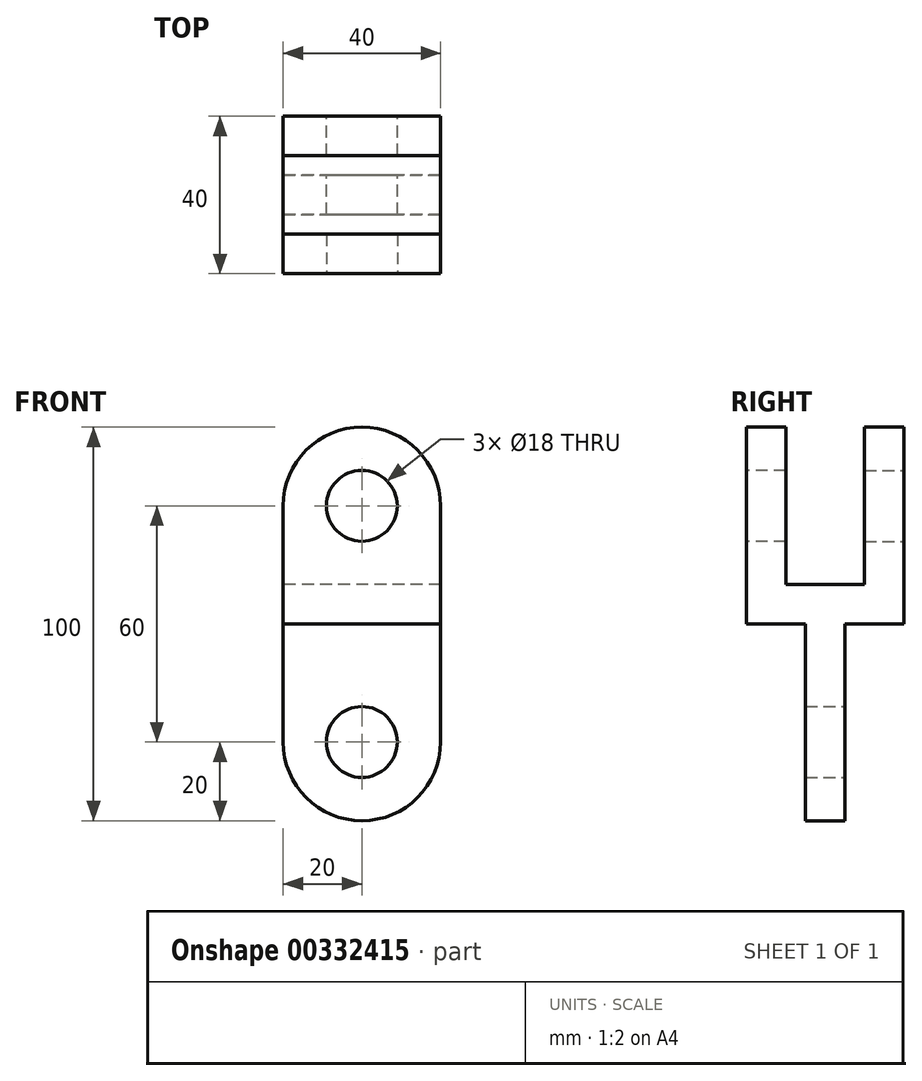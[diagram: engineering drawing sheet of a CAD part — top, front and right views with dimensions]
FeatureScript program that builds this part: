
annotation { "Feature Type Name" : "Feature", "Feature Type Description" : "" }
export const myFeature = defineFeature(function(context is Context, id is Id, definition is map)
    precondition{}
    {
        {
            var Q0;
            Q0=qCreatedBy(makeId("Front.planeOp"),FACE);
            var sketch = newSketch(context, id + "F0", { "sketchPlane" : qUnion([Q0])});
            skLineSegment(sketch, "E0.bottom", {"start": v(20, -15) * mm, "end": v(-20, -15) * mm});
            skLineSegment(sketch, "E0.top", {"start": v(20, 15) * mm, "end": v(-20, 15) * mm});
            skLineSegment(sketch, "E0.left", {"start": v(20, -15) * mm, "end": v(20, 15) * mm});
            skLineSegment(sketch, "E0.right", {"start": v(-20, -15) * mm, "end": v(-20, 15) * mm});
            skPoint(sketch, "E0.middle", {"position": v(0, 0) * mm});
            skArc(sketch, "E1", {"start": v(-20, -15) * mm, "mid": v(0, -35) * mm, "end": v(20, -15) * mm});
            skCircle(sketch, "E2", {"center": v(0, -15) * mm, "radius": 9 * mm});
            skPoint(sketch, "E3", {"position": v(215.53, -59.48) * mm});
            skSolve(sketch);
        }
        {
            var Q0;
            Q0 = qSketchRegion(id + "F0", true);
            extrude(context, id + "F1", {"entities" : qUnion([Q0]), "depth" : 10 * mm, "symmetric" : true});
        }
        {
            var Q0;
            Q0=makeQuery(id+"F1.opExtrude","SWEPT_FACE",FACE,{"disambiguationData":[OSD([sQuery(id+"F0.wireOp",EDGE,"E0.top")])]});
            var sketch = newSketch(context, id + "F2", { "sketchPlane" : qUnion([Q0])});
            skLineSegment(sketch, "E4.bottom", {"start": v(20, 20) * mm, "end": v(-20, 20) * mm});
            skLineSegment(sketch, "E4.top", {"start": v(20, -20) * mm, "end": v(-20, -20) * mm});
            skLineSegment(sketch, "E4.left", {"start": v(20, 20) * mm, "end": v(20, -20) * mm});
            skLineSegment(sketch, "E4.right", {"start": v(-20, 20) * mm, "end": v(-20, -20) * mm});
            skPoint(sketch, "E4.middle", {"position": v(0, 0) * mm});
            skSolve(sketch);
        }
        {
            var Q0;
            Q0 = qSketchRegion(id + "F2", true);
            extrude(context, id + "F3", {"entities" : qUnion([Q0]), "operationType" : NewBodyOperationType.ADD, "depth" : 10 * mm});
        }
        {
            var Q0;
            Q0=makeQuery(id+"F3.opExtrude","SWEPT_FACE",FACE,{"disambiguationData":[OSD([sQuery(id+"F2.wireOp",EDGE,"E4.top")])]});
            var sketch = newSketch(context, id + "F4", { "sketchPlane" : qUnion([Q0])});
            skLineSegment(sketch, "E5.bottom", {"start": v(-20, 45) * mm, "end": v(20, 45) * mm});
            skLineSegment(sketch, "E5.top", {"start": v(-20, 25) * mm, "end": v(20, 25) * mm});
            skLineSegment(sketch, "E5.left", {"start": v(-20, 45) * mm, "end": v(-20, 25) * mm});
            skLineSegment(sketch, "E5.right", {"start": v(20, 45) * mm, "end": v(20, 25) * mm});
            skArc(sketch, "E6", {"start": v(20, 45) * mm, "mid": v(0, 65) * mm, "end": v(-20, 45) * mm});
            skCircle(sketch, "E7", {"center": v(0, 45) * mm, "radius": 9 * mm});
            skSolve(sketch);
        }
        {
            var Q0;
            Q0 = qSketchRegion(id + "F4", true);
            extrude(context, id + "F5", {"entities" : qUnion([Q0]), "operationType" : NewBodyOperationType.ADD, "oppositeDirection" : true, "depth" : 10 * mm});
        }
        {
            var Q0;
            Q0=makeQuery(id+"F3.opExtrude","SWEPT_FACE",FACE,{"disambiguationData":[OSD([sQuery(id+"F2.wireOp",EDGE,"E4.bottom")])]});
            var sketch = newSketch(context, id + "F6", { "sketchPlane" : qUnion([Q0])});
            skLineSegment(sketch, "E8.bottom", {"start": v(-20, 45) * mm, "end": v(20, 45) * mm});
            skLineSegment(sketch, "E8.top", {"start": v(-20, 25) * mm, "end": v(20, 25) * mm});
            skLineSegment(sketch, "E8.left", {"start": v(-20, 45) * mm, "end": v(-20, 25) * mm});
            skLineSegment(sketch, "E8.right", {"start": v(20, 45) * mm, "end": v(20, 25) * mm});
            skArc(sketch, "E9", {"start": v(20, 45) * mm, "mid": v(0, 65) * mm, "end": v(-20, 45) * mm});
            skCircle(sketch, "E10", {"center": v(0, 45) * mm, "radius": 9 * mm});
            skSolve(sketch);
        }
        {
            var Q0;
            Q0 = qSketchRegion(id + "F6", true);
            extrude(context, id + "F7", {"entities" : qUnion([Q0]), "operationType" : NewBodyOperationType.ADD, "oppositeDirection" : true, "depth" : 10 * mm});
        }
    });
